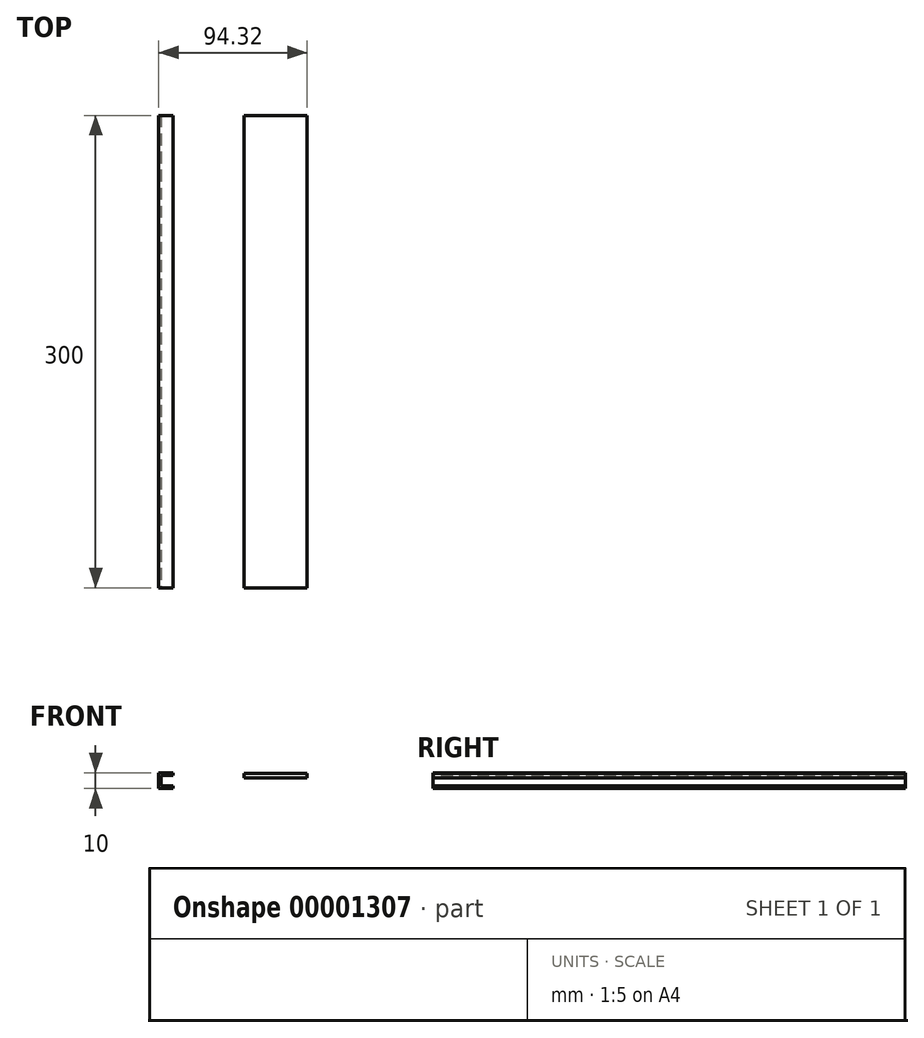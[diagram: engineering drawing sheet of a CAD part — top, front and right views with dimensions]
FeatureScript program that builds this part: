
annotation { "Feature Type Name" : "Feature", "Feature Type Description" : "" }
export const myFeature = defineFeature(function(context is Context, id is Id, definition is map)
    precondition{}
    {
        {
            var Q0;
            Q0=qCreatedBy(makeId("Front.planeOp"),FACE);
            var sketch = newSketch(context, id + "F0", { "sketchPlane" : qUnion([Q0])});
            skLineSegment(sketch, "E0.bottom", {"start": v(-53.07, -61.9) * mm, "end": v(-13.07, -61.9) * mm});
            skLineSegment(sketch, "E0.top", {"start": v(-53.07, -64.9) * mm, "end": v(-13.07, -64.9) * mm});
            skLineSegment(sketch, "E0.left", {"start": v(-53.07, -61.9) * mm, "end": v(-53.07, -64.9) * mm});
            skLineSegment(sketch, "E0.right", {"start": v(-13.07, -61.9) * mm, "end": v(-13.07, -64.9) * mm});
            skSolve(sketch);
        }
        {
            var Q0;
            Q0=makeQuery(id+"F0.imprint","IMPRINT",FACE,{"disambiguationData":[TD([[makeQuery(id+"F0.imprint","IMPRINT",EDGE,{"derivedFrom":sQuery(id+"F0.wireOp",EDGE,"E0.bottom")}),-1.0]])]});
            extrude(context, id + "F1", {"entities" : qUnion([Q0]), "oppositeDirection" : true, "depth" : 300 * mm, "offsetDistance" : 25 * mm});
        }
        {
            var Q0;
            Q0=qCreatedBy(makeId("Front.planeOp"),FACE);
            var sketch = newSketch(context, id + "F2", { "sketchPlane" : qUnion([Q0])});
            skLineSegment(sketch, "E1.bottom", {"start": v(-107.4, -61.57) * mm, "end": v(-98.4, -61.57) * mm});
            skLineSegment(sketch, "E1.top", {"start": v(-107.4, -71.57) * mm, "end": v(-98.4, -71.57) * mm});
            skLineSegment(sketch, "E1.left", {"start": v(-107.4, -61.57) * mm, "end": v(-107.4, -71.57) * mm});
            skLineSegment(sketch, "E1.right", {"start": v(-98.4, -61.57) * mm, "end": v(-98.4, -71.57) * mm});
            skLineSegment(sketch, "E2.bottom", {"start": v(-98.4, -63.17) * mm, "end": v(-105.8, -63.17) * mm});
            skLineSegment(sketch, "E2.top", {"start": v(-98.4, -69.97) * mm, "end": v(-105.8, -69.97) * mm});
            skLineSegment(sketch, "E2.left", {"start": v(-98.4, -63.17) * mm, "end": v(-98.4, -69.97) * mm});
            skLineSegment(sketch, "E2.right", {"start": v(-105.8, -63.17) * mm, "end": v(-105.8, -69.97) * mm});
            skSolve(sketch);
        }
        {
            var Q0;
            {var subQ1=sQuery(id+"F2.wireOp",EDGE,"E1.bottom");Q0=makeQuery(id+"F2.imprint","IMPRINT",FACE,{"disambiguationData":[TD([[makeQuery(id+"F2.imprint","IMPRINT",EDGE,{"derivedFrom":subQ1}),-1.0]])]});}
            extrude(context, id + "F3", {"entities" : qUnion([Q0]), "oppositeDirection" : true, "depth" : 300 * mm, "offsetDistance" : 25 * mm});
        }
    });
